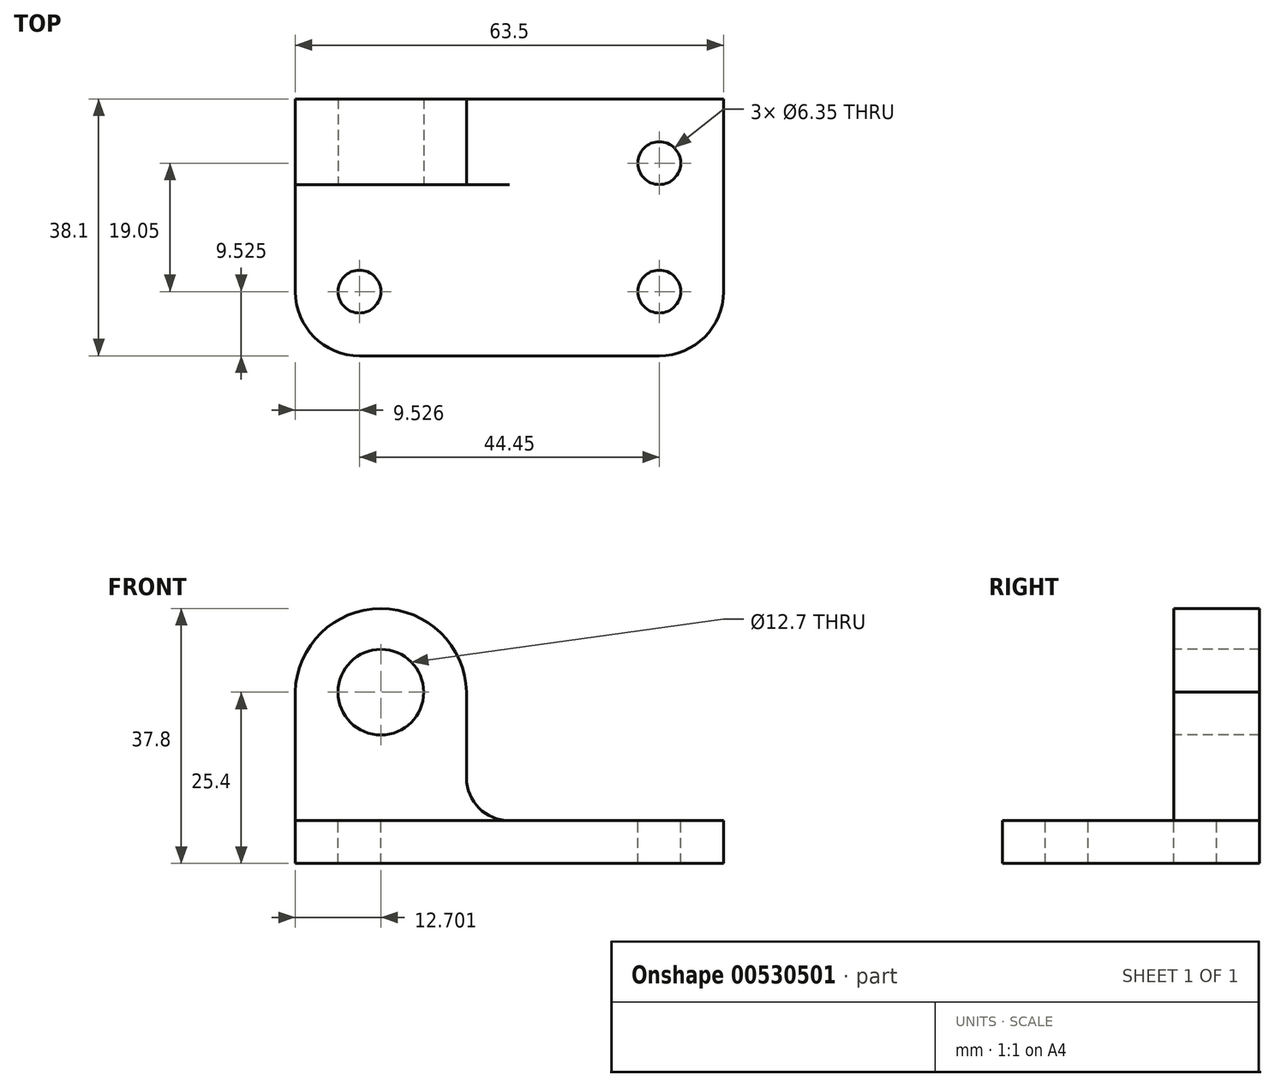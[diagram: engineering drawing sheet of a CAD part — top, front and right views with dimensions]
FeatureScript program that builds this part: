
annotation { "Feature Type Name" : "Feature", "Feature Type Description" : "" }
export const myFeature = defineFeature(function(context is Context, id is Id, definition is map)
    precondition{}
    {
        {
            var Q0;
            Q0=qCreatedBy(makeId("Top.planeOp"),FACE);
            var sketch = newSketch(context, id + "F0", { "sketchPlane" : qUnion([Q0])});
            skLineSegment(sketch, "E0", {"start": v(137.44, -78.24) * mm, "end": v(137.44, -186.45) * mm});
            skLineSegment(sketch, "E1.bottom", {"start": v(-70.4, 38.1) * mm, "end": v(-6.9, 38.1) * mm});
            skLineSegment(sketch, "E1.top", {"start": v(-70.4, 0) * mm, "end": v(-6.9, 0) * mm});
            skLineSegment(sketch, "E1.left", {"start": v(-70.4, 38.1) * mm, "end": v(-70.4, 0) * mm});
            skLineSegment(sketch, "E1.right", {"start": v(-6.9, 38.1) * mm, "end": v(-6.9, 0) * mm});
            skSolve(sketch);
        }
        {
            var Q0;
            Q0 = qSketchRegion(id + "F0", true);
            extrude(context, id + "F1", {"entities" : qUnion([Q0]), "depth" : 6.35 * mm, "offsetDistance" : 25.4 * mm});
        }
        {
            var Q0;
            Q0=makeQuery(id+"F1.opExtrude","CAP_FACE",FACE,{"disambiguationData":[OSD([sQuery(id+"F0.wireOp",EDGE,"E1.bottom"),sQuery(id+"F0.wireOp",EDGE,"E1.top"),sQuery(id+"F0.wireOp",EDGE,"E1.left"),sQuery(id+"F0.wireOp",EDGE,"E1.right")])],"isStart":false});
            var sketch = newSketch(context, id + "F2", { "sketchPlane" : qUnion([Q0])});
            skCircle(sketch, "E2", {"center": v(-16.43, 28.57) * mm, "radius": 3.18 * mm});
            skCircle(sketch, "E3", {"center": v(-16.43, 9.53) * mm, "radius": 3.18 * mm});
            skCircle(sketch, "E4", {"center": v(-60.88, 9.53) * mm, "radius": 3.18 * mm});
            skSolve(sketch);
        }
        {
            var Q0;
            Q0=makeQuery(id+"F2.imprint","IMPRINT",FACE,{"disambiguationData":[TD([[makeQuery(id+"F2.imprint","IMPRINT",EDGE,{"derivedFrom":sQuery(id+"F2.wireOp",EDGE,"E2")}),1.0]])]});
            var Q1;
            Q1=makeQuery(id+"F2.imprint","IMPRINT",FACE,{"disambiguationData":[TD([[makeQuery(id+"F2.imprint","IMPRINT",EDGE,{"derivedFrom":sQuery(id+"F2.wireOp",EDGE,"E3")}),1.0]])]});
            var Q2;
            Q2=makeQuery(id+"F2.imprint","IMPRINT",FACE,{"disambiguationData":[TD([[makeQuery(id+"F2.imprint","IMPRINT",EDGE,{"derivedFrom":sQuery(id+"F2.wireOp",EDGE,"E4")}),1.0]])]});
            extrude(context, id + "F3", {"entities" : qUnion([Q0, Q1, Q2]), "operationType" : NewBodyOperationType.REMOVE, "oppositeDirection" : true, "depth" : 25.4 * mm, "offsetDistance" : 25.4 * mm});
        }
        {
            var Q0;
            Q0=makeQuery(id+"F1.opExtrude","CAP_FACE",FACE,{"disambiguationData":[OSD([sQuery(id+"F0.wireOp",EDGE,"E1.bottom"),sQuery(id+"F0.wireOp",EDGE,"E1.top"),sQuery(id+"F0.wireOp",EDGE,"E1.left"),sQuery(id+"F0.wireOp",EDGE,"E1.right")])],"isStart":false});
            var sketch = newSketch(context, id + "F4", { "sketchPlane" : qUnion([Q0])});
            skLineSegment(sketch, "E5", {"start": v(-70.4, 25.4) * mm, "end": v(-45, 25.4) * mm});
            skLineSegment(sketch, "E6", {"start": v(-45, 25.4) * mm, "end": v(-45, 38.1) * mm});
            skLineSegment(sketch, "E7", {"start": v(-45, 38.1) * mm, "end": v(-70.4, 38.1) * mm});
            skLineSegment(sketch, "E8", {"start": v(-70.4, 38.1) * mm, "end": v(-70.4, 25.4) * mm});
            skSolve(sketch);
        }
        {
            var Q0;
            Q0 = qSketchRegion(id + "F4", true);
            extrude(context, id + "F5", {"entities" : qUnion([Q0]), "operationType" : NewBodyOperationType.ADD, "depth" : 31.75 * mm, "offsetDistance" : 25.4 * mm});
        }
        {
            var Q0;
            Q0=makeQuery(id+"F5.opExtrude","SWEPT_FACE",FACE,{"disambiguationData":[OSD([sQuery(id+"F4.wireOp",EDGE,"E5")])]});
            var sketch = newSketch(context, id + "F6", { "sketchPlane" : qUnion([Q0])});
            skCircle(sketch, "E9", {"center": v(-57.7, 25.4) * mm, "radius": 6.35 * mm});
            skArc(sketch, "E10", {"start": v(-45, 25.4) * mm, "mid": v(-57.7, 37.8) * mm, "end": v(-70.4, 25.4) * mm});
            skSolve(sketch);
        }
        {
            var Q0;
            Q0 = qSketchRegion(id + "F6", true);
            var Q1;
            {var subQ0=sQuery(id+"F6.wireOp",EDGE,"E10");Q1=makeQuery(id+"F6.imprint","IMPRINT",FACE,{"disambiguationData":[TD([[makeQuery(id+"F6.imprint","IMPRINT",EDGE,{"derivedFrom":subQ0}),-1.0]])]});}
            extrude(context, id + "F7", {"entities" : qUnion([Q0, Q1]), "operationType" : NewBodyOperationType.REMOVE, "oppositeDirection" : true, "depth" : 25.4 * mm, "offsetDistance" : 25.4 * mm});
        }
        {
            var Q0;
            Q0=makeQuery(id+"F1.opExtrude","SWEPT_EDGE",EDGE,{"disambiguationData":[OSD([sQuery(id+"F0.wireOp",EDGE,"E1.top"),sQuery(id+"F0.wireOp",EDGE,"E1.right")])]});
            var Q1;
            Q1=makeQuery(id+"F1.opExtrude","SWEPT_EDGE",EDGE,{"disambiguationData":[OSD([sQuery(id+"F0.wireOp",EDGE,"E1.top"),sQuery(id+"F0.wireOp",EDGE,"E1.left")])]});
            fillet(context, id + "F8", {"entities" : qUnion([Q0, Q1]), "radius" : 9.52 * mm, "tangentPropagation" : true, "allowEdgeOverflow" : false});
        }
        {
            var Q0;
            Q0=makeQuery(id+"F5.opExtrude","SWEPT_FACE",FACE,{"disambiguationData":[OSD([sQuery(id+"F4.wireOp",EDGE,"E6")])]});
            var sketch = newSketch(context, id + "F9", { "sketchPlane" : qUnion([Q0])});
            skLineSegment(sketch, "E11", {"start": v(38.1, 6.35) * mm, "end": v(25.4, 6.35) * mm});
            skLineSegment(sketch, "E12", {"start": v(25.4, 6.35) * mm, "end": v(25.4, 19.05) * mm});
            skLineSegment(sketch, "E13", {"start": v(25.4, 19.05) * mm, "end": v(38.1, 19.05) * mm});
            skLineSegment(sketch, "E14", {"start": v(38.1, 19.05) * mm, "end": v(35.99, 18.08) * mm});
            skLineSegment(sketch, "E15", {"start": v(38.1, 6.35) * mm, "end": v(38.1, 19.05) * mm});
            skSolve(sketch);
        }
        {
            var Q0;
            Q0 = qSketchRegion(id + "F9", true);
            extrude(context, id + "F10", {"entities" : qUnion([Q0]), "operationType" : NewBodyOperationType.ADD, "depth" : 12.7 * mm, "offsetDistance" : 25.4 * mm});
        }
        {
            var Q0;
            Q0=makeQuery(id+"F10.boolean.opBoolean","MERGE",FACE,{"derivedFrom":[makeQuery(id+"F5.opExtrude","SWEPT_FACE",FACE,{"disambiguationData":[OSD([sQuery(id+"F4.wireOp",EDGE,"E5")])]}),makeQuery(id+"F10.opExtrude","SWEPT_FACE",FACE,{"disambiguationData":[OSD([sQuery(id+"F9.wireOp",EDGE,"E12")])]})]});
            var sketch = newSketch(context, id + "F11", { "sketchPlane" : qUnion([Q0])});
            skLineSegment(sketch, "E16", {"start": v(-45, 19.05) * mm, "end": v(-45, 6.35) * mm});
            skPoint(sketch, "E17.centerSnap0", {"position": v(-32.3, 12.7) * mm});
            skCircle(sketch, "E18", {"center": v(-38.66, 12.7) * mm, "radius": 6.35 * mm});
            skPoint(sketch, "E18.centerSnap0", {"position": v(-38.66, 19.05) * mm});
            skSolve(sketch);
        }
        {
            var Q0;
            {var subQ0=sQuery(id+"F11.wireOp",EDGE,"E18");var subQ1=sQuery(id+"F9.wireOp",EDGE,"E12");var subQ4=makeQuery(id+"F10.opExtrude","CAP_EDGE",EDGE,{"disambiguationData":[OSD([subQ1])],"isStart":false});var subQ5=makeQuery(id+"F11.imprint","INTERSECT",VERTEX,{"derivedFrom":[subQ4,subQ0]});Q0=makeQuery(id+"F11.imprint","IMPRINT",FACE,{"disambiguationData":[TD([[makeQuery(id+"F11.imprint","IMPRINT",EDGE,{"disambiguationData":[TD([[subQ5,-1.0]])],"derivedFrom":subQ0}),-1.0]])]});}
            var Q1;
            {var subQ0=sQuery(id+"F11.wireOp",EDGE,"E16");var subQ5=sQuery(id+"F11.wireOp",EDGE,"E18");var subQ6=makeQuery(id+"F11.imprint","INTERSECT",VERTEX,{"derivedFrom":[subQ0,subQ5]});Q1=makeQuery(id+"F11.imprint","IMPRINT",FACE,{"disambiguationData":[TD([[makeQuery(id+"F11.imprint","IMPRINT",EDGE,{"disambiguationData":[TD([[subQ6,1.0]])],"derivedFrom":subQ5}),-1.0]])]});}
            var Q2;
            {var subQ0=sQuery(id+"F11.wireOp",EDGE,"E18");var subQ1=sQuery(id+"F9.wireOp",EDGE,"E12");var subQ2=makeQuery(id+"F10.opExtrude","CAP_EDGE",EDGE,{"disambiguationData":[OSD([subQ1])],"isStart":false});var subQ3=makeQuery(id+"F11.imprint","INTERSECT",VERTEX,{"derivedFrom":[subQ2,subQ0]});Q2=makeQuery(id+"F11.imprint","IMPRINT",FACE,{"disambiguationData":[TD([[makeQuery(id+"F11.imprint","IMPRINT",EDGE,{"disambiguationData":[TD([[subQ3,1.0]])],"derivedFrom":subQ0}),-1.0]])]});}
            var Q3;
            {var subQ0=sQuery(id+"F11.wireOp",EDGE,"E18");var subQ5=makeQuery(id+"F11.imprint","INTERSECT",VERTEX,{"derivedFrom":[sQuery(id+"F11.wireOp",EDGE,"E16"),subQ0]});Q3=makeQuery(id+"F11.imprint","IMPRINT",FACE,{"disambiguationData":[TD([[makeQuery(id+"F11.imprint","IMPRINT",EDGE,{"disambiguationData":[TD([[subQ5,-1.0]])],"derivedFrom":subQ0}),1.0]])]});}
            extrude(context, id + "F12", {"entities" : qUnion([Q0, Q1, Q2, Q3]), "operationType" : NewBodyOperationType.REMOVE, "oppositeDirection" : true, "depth" : 25.4 * mm, "offsetDistance" : 25.4 * mm});
        }
    });
